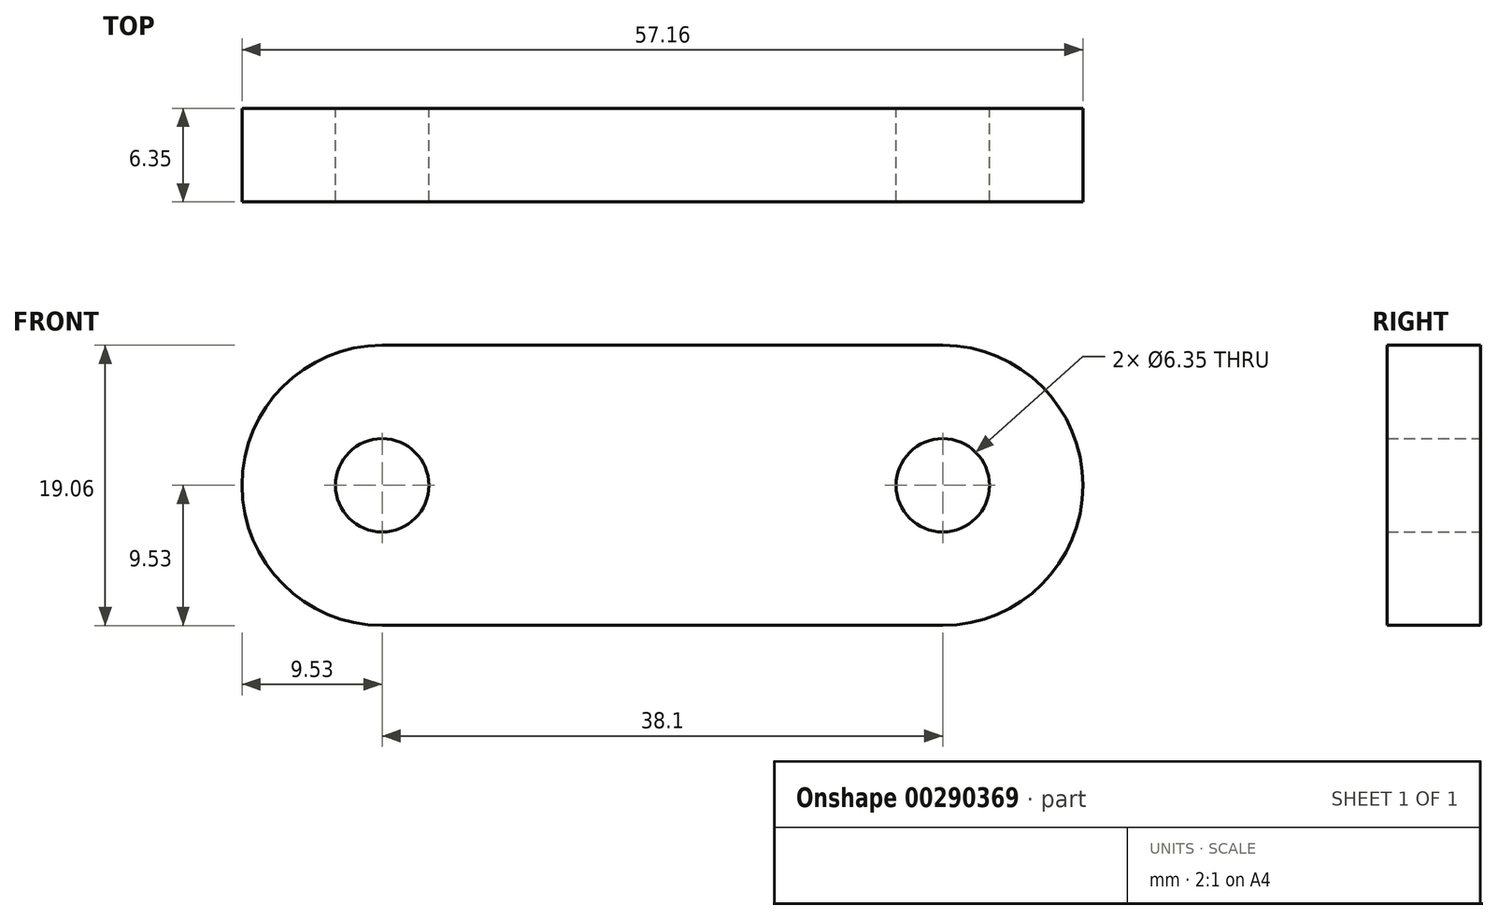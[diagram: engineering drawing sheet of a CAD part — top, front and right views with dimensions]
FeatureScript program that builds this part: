
annotation { "Feature Type Name" : "Feature", "Feature Type Description" : "" }
export const myFeature = defineFeature(function(context is Context, id is Id, definition is map)
    precondition{}
    {
        {
            var Q0;
            Q0=qCreatedBy(makeId("Front.planeOp"),FACE);
            var sketch = newSketch(context, id + "F0", { "sketchPlane" : qUnion([Q0])});
            skLineSegment(sketch, "E0.bottom", {"start": v(-19.05, 9.53) * mm, "end": v(19.05, 9.52) * mm});
            skLineSegment(sketch, "E0.top", {"start": v(-19.05, -9.52) * mm, "end": v(19.05, -9.53) * mm});
            skLineSegment(sketch, "E0.left", {"start": v(-19.05, 9.53) * mm, "end": v(-19.05, -9.53) * mm});
            skLineSegment(sketch, "E0.right", {"start": v(19.05, 9.53) * mm, "end": v(19.05, -9.53) * mm});
            skPoint(sketch, "E1", {"position": v(0, 9.53) * mm});
            skPoint(sketch, "E2", {"position": v(19.05, 0) * mm});
            skPoint(sketch, "E3", {"position": v(0, 0) * mm});
            skPoint(sketch, "E4", {"position": v(-19.05, 0) * mm});
            skCircle(sketch, "E5", {"center": v(-19.05, 0) * mm, "radius": 3.18 * mm});
            skCircle(sketch, "E6", {"center": v(19.05, 0) * mm, "radius": 3.17 * mm});
            skArc(sketch, "E7", {"start": v(-19.05, 9.53) * mm, "mid": v(-28.58, 0) * mm, "end": v(-19.05, -9.52) * mm});
            skArc(sketch, "E8", {"start": v(19.05, -9.53) * mm, "mid": v(28.58, 0) * mm, "end": v(19.05, 9.52) * mm});
            skSolve(sketch);
        }
        {
            var Q0;
            Q0=qSketchRegion(id+"F0",true);
            extrude(context, id + "F1", {"entities" : qUnion([Q0]), "depth" : 6.35 * mm});
        }
    });
